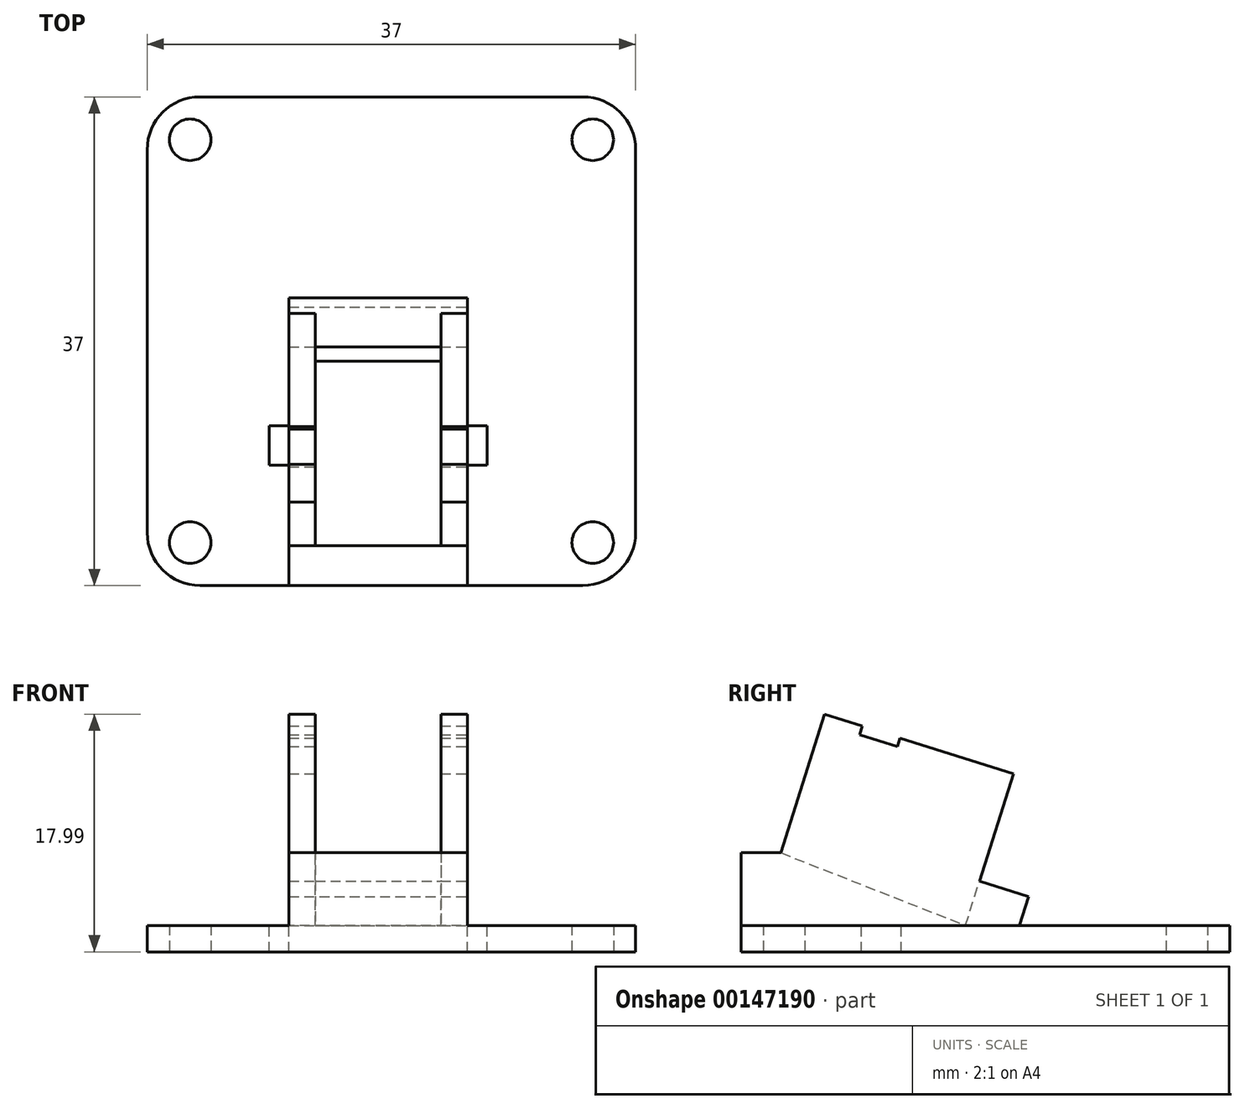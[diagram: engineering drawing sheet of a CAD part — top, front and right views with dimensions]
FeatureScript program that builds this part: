
annotation { "Feature Type Name" : "Feature", "Feature Type Description" : "" }
export const myFeature = defineFeature(function(context is Context, id is Id, definition is map)
    precondition{}
    {
        {
            var Q0;
            Q0=qCreatedBy(makeId("Top.planeOp"),FACE);
            var sketch = newSketch(context, id + "F0", { "sketchPlane" : qUnion([Q0])});
            skLineSegment(sketch, "E0.bottom", {"start": v(18.5, 18.5) * mm, "end": v(-18.5, 18.5) * mm});
            skLineSegment(sketch, "E0.top", {"start": v(18.5, -18.5) * mm, "end": v(-18.5, -18.5) * mm});
            skLineSegment(sketch, "E0.left", {"start": v(18.5, 18.5) * mm, "end": v(18.5, -18.5) * mm});
            skLineSegment(sketch, "E0.right", {"start": v(-18.5, 18.5) * mm, "end": v(-18.5, -18.5) * mm});
            skPoint(sketch, "E0.middle", {"position": v(0, 0) * mm});
            skCircle(sketch, "E1", {"center": v(-15.25, 15.25) * mm, "radius": 1.57 * mm});
            skCircle(sketch, "E2.MirrorC", {"center": v(15.25, 15.25) * mm, "radius": 1.57 * mm});
            skCircle(sketch, "E3.MirrorC", {"center": v(-15.25, -15.25) * mm, "radius": 1.57 * mm});
            skCircle(sketch, "E4.MirrorC", {"center": v(15.25, -15.25) * mm, "radius": 1.57 * mm});
            skSolve(sketch);
        }
        {
            var Q0;
            Q0 = qSketchRegion(id + "F0", true);
            extrude(context, id + "F1", {"entities" : qUnion([Q0]), "depth" : 2 * mm});
        }
        {
            var Q0;
            Q0=makeQuery(id+"F1.opExtrude","SWEPT_FACE",FACE,{"disambiguationData":[OSD([sQuery(id+"F0.wireOp",EDGE,"E0.left")])]});
            var sketch = newSketch(context, id + "F2", { "sketchPlane" : qUnion([Q0])});
            skLineSegment(sketch, "E5", {"start": v(-18.5, 2) * mm, "end": v(-18.5, 7.5) * mm});
            skLineSegment(sketch, "E6", {"start": v(-18.5, 7.5) * mm, "end": v(-15.5, 7.5) * mm});
            skLineSegment(sketch, "E7", {"start": v(-15.5, 7.5) * mm, "end": v(-12.19, 17.99) * mm});
            skLineSegment(sketch, "E8", {"start": v(-12.19, 17.99) * mm, "end": v(-9.33, 17.09) * mm});
            skLineSegment(sketch, "E9", {"start": v(-9.33, 17.09) * mm, "end": v(-9.53, 16.45) * mm});
            skLineSegment(sketch, "E10", {"start": v(-9.53, 16.45) * mm, "end": v(-6.67, 15.54) * mm});
            skLineSegment(sketch, "E11", {"start": v(-6.67, 15.54) * mm, "end": v(-6.47, 16.18) * mm});
            skLineSegment(sketch, "E12", {"start": v(-6.47, 16.18) * mm, "end": v(2.12, 13.47) * mm});
            skLineSegment(sketch, "E13", {"start": v(2.12, 13.47) * mm, "end": v(-0.44, 5.37) * mm});
            skLineSegment(sketch, "E14", {"start": v(-0.44, 5.37) * mm, "end": v(3.28, 4.2) * mm});
            skLineSegment(sketch, "E15", {"start": v(3.28, 4.2) * mm, "end": v(2.58, 2) * mm});
            skLineSegment(sketch, "E16", {"start": v(-0.44, 5.37) * mm, "end": v(-1.5, 2) * mm});
            skLineSegment(sketch, "E17", {"start": v(-1.5, 2) * mm, "end": v(-15.5, 7.5) * mm});
            skSolve(sketch);
        }
        {
            var Q0;
            Q0 = qSketchRegion(id + "F2", true);
            var Q1;
            {var subQ0=sQuery(id+"F2.wireOp",EDGE,"E5");Q1=makeQuery(id+"F2.imprint","IMPRINT",FACE,{"disambiguationData":[TD([[makeQuery(id+"F2.imprint","IMPRINT",EDGE,{"derivedFrom":subQ0}),-1.0]])]});}
            var Q2;
            Q2=makeQuery(id+"F2.imprint","IMPRINT",FACE,{"disambiguationData":[TD([[makeQuery(id+"F2.imprint","IMPRINT",EDGE,{"derivedFrom":sQuery(id+"F2.wireOp",EDGE,"E14")}),-1.0]])]});
            extrude(context, id + "F3", {"entities" : qUnion([Q0, Q1, Q2]), "operationType" : NewBodyOperationType.ADD, "oppositeDirection" : true, "depth" : 26.25 * mm});
        }
        {
            var Q0;
            Q0=makeQuery(id+"F2.imprint","IMPRINT",FACE,{"disambiguationData":[TD([[makeQuery(id+"F2.imprint","IMPRINT",EDGE,{"derivedFrom":sQuery(id+"F2.wireOp",EDGE,"E7")}),-1.0]])]});
            extrude(context, id + "F4", {"entities" : qUnion([Q0]), "operationType" : NewBodyOperationType.REMOVE, "oppositeDirection" : true, "depth" : 24.25 * mm});
        }
        {
            var Q0;
            Q0 = qSketchRegion(id + "F2", true);
            var Q1;
            {var subQ0=sQuery(id+"F2.wireOp",EDGE,"E5");Q1=makeQuery(id+"F2.imprint","IMPRINT",FACE,{"disambiguationData":[TD([[makeQuery(id+"F2.imprint","IMPRINT",EDGE,{"derivedFrom":subQ0}),-1.0]])]});}
            var Q2;
            Q2=makeQuery(id+"F2.imprint","IMPRINT",FACE,{"disambiguationData":[TD([[makeQuery(id+"F2.imprint","IMPRINT",EDGE,{"derivedFrom":sQuery(id+"F2.wireOp",EDGE,"E14")}),-1.0]])]});
            extrude(context, id + "F5", {"entities" : qUnion([Q0, Q1, Q2]), "operationType" : NewBodyOperationType.ADD, "oppositeDirection" : true, "depth" : 14.75 * mm});
        }
        {
            var Q0;
            Q0 = qSketchRegion(id + "F2", true);
            var Q1;
            {var subQ0=sQuery(id+"F2.wireOp",EDGE,"E5");Q1=makeQuery(id+"F2.imprint","IMPRINT",FACE,{"disambiguationData":[TD([[makeQuery(id+"F2.imprint","IMPRINT",EDGE,{"derivedFrom":subQ0}),-1.0]])]});}
            var Q2;
            Q2=makeQuery(id+"F2.imprint","IMPRINT",FACE,{"disambiguationData":[TD([[makeQuery(id+"F2.imprint","IMPRINT",EDGE,{"derivedFrom":sQuery(id+"F2.wireOp",EDGE,"E14")}),-1.0]])]});
            extrude(context, id + "F6", {"entities" : qUnion([Q0, Q1, Q2]), "operationType" : NewBodyOperationType.REMOVE, "oppositeDirection" : true, "depth" : 12.75 * mm});
        }
        {
            var Q0;
            Q0=makeQuery(id+"F3.boolean.opBoolean","MERGE",EDGE,{"derivedFrom":[makeQuery(id+"F1.opExtrude","SWEPT_EDGE",EDGE,{"disambiguationData":[OSD([sQuery(id+"F0.wireOp",EDGE,"E0.top"),sQuery(id+"F0.wireOp",EDGE,"E0.left")])]}),makeQuery(id+"F3.opExtrude","CAP_EDGE",EDGE,{"disambiguationData":[OSD([sQuery(id+"F2.wireOp",EDGE,"E5")])],"isStart":true})]});
            var Q1;
            Q1=makeQuery(id+"F1.opExtrude","SWEPT_EDGE",EDGE,{"disambiguationData":[OSD([sQuery(id+"F0.wireOp",EDGE,"E0.bottom"),sQuery(id+"F0.wireOp",EDGE,"E0.left")])]});
            var Q2;
            Q2=makeQuery(id+"F1.opExtrude","SWEPT_EDGE",EDGE,{"disambiguationData":[OSD([sQuery(id+"F0.wireOp",EDGE,"E0.bottom"),sQuery(id+"F0.wireOp",EDGE,"E0.right")])]});
            var Q3;
            Q3=makeQuery(id+"F1.opExtrude","SWEPT_EDGE",EDGE,{"disambiguationData":[OSD([sQuery(id+"F0.wireOp",EDGE,"E0.top"),sQuery(id+"F0.wireOp",EDGE,"E0.right")])]});
            fillet(context, id + "F7", {"entities" : qUnion([Q0, Q1, Q2, Q3]), "radius" : 4 * mm, "tangentPropagation" : true, "allowEdgeOverflow" : false});
        }
        {
            var Q0;
            {var subQ0=sQuery(id+"F0.wireOp",EDGE,"E0.left");Q0=makeQuery(id+"F6.boolean.opBoolean","MERGE",FACE,{"derivedFrom":[makeQuery(id+"F1.opExtrude","CAP_FACE",FACE,{"disambiguationData":[OSD([sQuery(id+"F0.wireOp",EDGE,"E0.bottom"),sQuery(id+"F0.wireOp",EDGE,"E0.top"),subQ0,sQuery(id+"F0.wireOp",EDGE,"E0.right"),sQuery(id+"F0.wireOp",EDGE,"E1"),sQuery(id+"F0.wireOp",EDGE,"E2.MirrorC"),sQuery(id+"F0.wireOp",EDGE,"E3.MirrorC"),sQuery(id+"F0.wireOp",EDGE,"E4.MirrorC")])],"isStart":false}),makeQuery(id+"F6.opExtrude","SWEPT_FACE",FACE,{"disambiguationData":[OSD([subQ0])]})]});}
            var sketch = newSketch(context, id + "F8", { "sketchPlane" : qUnion([Q0])});
            skLineSegment(sketch, "E18.bottom", {"start": v(-7.75, -6.4) * mm, "end": v(-9.25, -6.4) * mm});
            skLineSegment(sketch, "E18.top", {"start": v(-7.75, -9.4) * mm, "end": v(-9.25, -9.4) * mm});
            skLineSegment(sketch, "E18.left", {"start": v(-7.75, -6.4) * mm, "end": v(-7.75, -9.4) * mm});
            skLineSegment(sketch, "E18.right", {"start": v(-9.25, -6.4) * mm, "end": v(-9.25, -9.4) * mm});
            skLineSegment(sketch, "E19.bottom", {"start": v(5.75, -6.4) * mm, "end": v(7.25, -6.4) * mm});
            skLineSegment(sketch, "E19.top", {"start": v(5.75, -9.4) * mm, "end": v(7.25, -9.4) * mm});
            skLineSegment(sketch, "E19.left", {"start": v(5.75, -6.4) * mm, "end": v(5.75, -9.4) * mm});
            skLineSegment(sketch, "E19.right", {"start": v(7.25, -6.4) * mm, "end": v(7.25, -9.4) * mm});
            skSolve(sketch);
        }
        {
            var Q0;
            Q0 = qSketchRegion(id + "F8", true);
            extrude(context, id + "F9", {"entities" : qUnion([Q0]), "operationType" : NewBodyOperationType.REMOVE, "oppositeDirection" : true, "depth" : 25 * mm});
        }
    });
